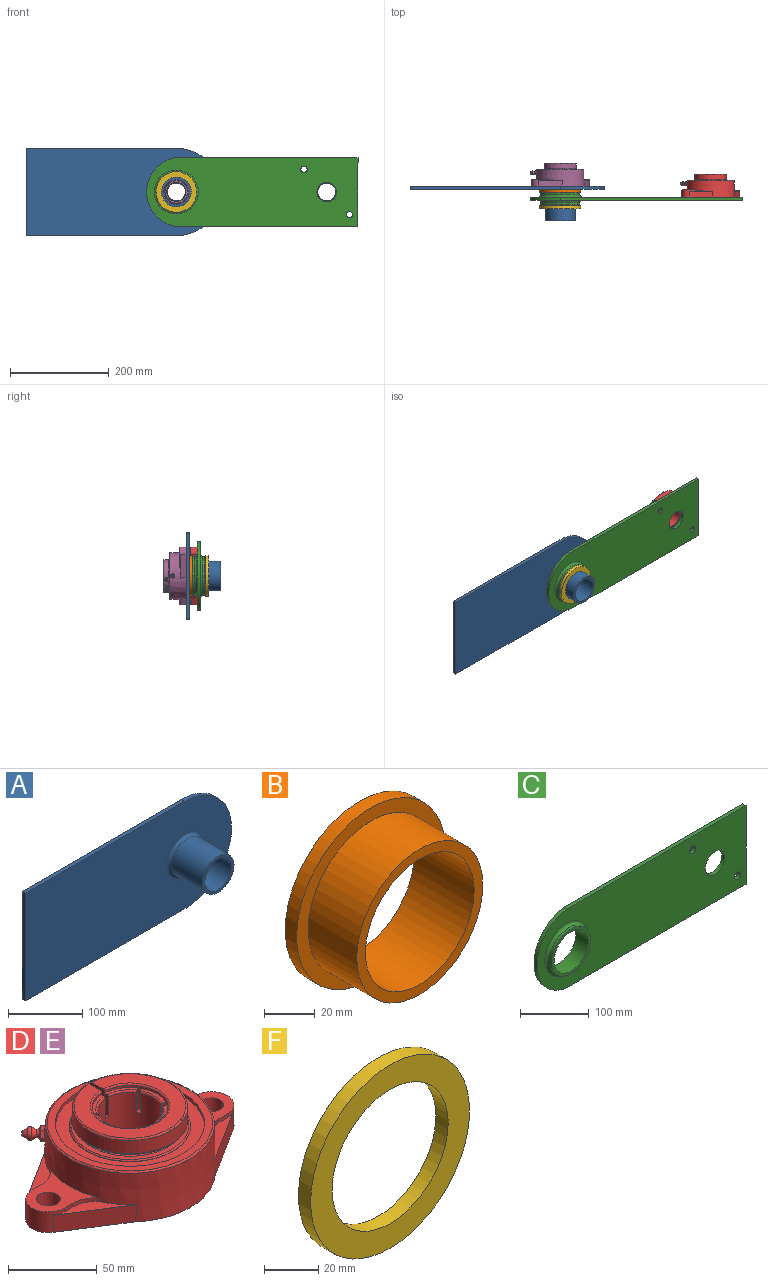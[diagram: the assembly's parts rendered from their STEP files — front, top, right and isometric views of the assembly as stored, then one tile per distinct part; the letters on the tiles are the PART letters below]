
ASSEMBLY  parts=6 mates=12
PART A: 10 faces, bbox 393.7x69.9x177.8 mm
  f0: plane 304.8x6.35mm, normal (0,0,-1), area 1935.5mm2, adj f1,f3,f4,f5
  f1: cylinder r=88.9mm len=177.8mm, axis (0,1,0), area 1773.5mm2, adj f0,f2,f4,f5
  f2: plane 304.8x6.35mm, normal (0,0,1), area 1935.5mm2, adj f1,f3,f4,f5
  f3: plane 177.8x6.35mm, normal (-1,0,0), area 1129mm2, adj f0,f2,f4,f5
  f4: plane 393.7x177.8mm, normal (0,-1,0), area 62775.8mm2, adj f0,f1,f2,f3,f9
  f5: plane 393.7x177.8mm, normal (0,1,0), area 64580.9mm2, adj f0,f1,f2,f3,f6
  f6: cylinder r=25.4mm len=69.85mm, axis (0,1,0), area 11147.6mm2, adj f5,f8
  f7: cylinder r=30.16mm len=60.33mm, axis (0,1,0), area 11131.7mm2, adj f8,f9
  f8: plane 60.33x60.33mm, normal (0,-1,0), area 831.3mm2, adj f6,f7
  f9: torus R=34.92mm, axis (0,-1,0), area 1499.1mm2, adj f4,f7
PART B: 6 faces, bbox 82.6x33.3x82.6 mm
  f0: cylinder r=30.16mm len=60.33mm, axis (0,1,0), area 6318mm2, adj f2,f3
  f1: cylinder r=34.92mm len=69.85mm, axis (0,1,0), area 5922.1mm2, adj f2,f5
  f2: plane 69.85x69.85mm, normal (0,-1,0), area 973.8mm2, adj f0,f1
  f3: plane 82.55x82.55mm, normal (0,1,0), area 2494mm2, adj f0,f4
  f4: cylinder r=41.27mm len=82.55mm, axis (0,1,0), area 1646.8mm2, adj f3,f5
  f5: plane 82.55x82.55mm, normal (0,-1,0), area 1520.1mm2, adj f1,f4
PART C: 16 faces, bbox 428.6x25.4x139.7 mm
  f0: plane 139.7x6.35mm, normal (1,0,0), area 887.1mm2, adj f1,f4,f5,f6
  f1: plane 368.3x6.35mm, normal (0,0,1), area 2338.7mm2, adj f0,f2,f5,f6
  f2: cylinder r=70.6mm len=139.7mm, axis (0,1,0), area 1277.5mm2, adj f1,f4,f5,f6
  f3: cylinder r=19.84mm len=39.69mm, axis (0,1,0), area 791.7mm2, adj f5,f6
  f4: plane 368.3x6.35mm, normal (0,0,-1), area 2338.7mm2, adj f0,f2,f5,f6
  f5: plane 428.63x139.7mm, normal (0,-1,0), area 50137.8mm2, adj f0,f1,f2,f3,f4,f13,f14,f15
  f6: plane 428.63x139.7mm, normal (0,1,0), area 50137.8mm2, adj f0,f1,f2,f3,f4,f12,f14,f15
  f7: cylinder r=39.69mm len=79.38mm, axis (0,1,0), area 1187.6mm2, adj f11,f12
  f8: cylinder r=34.92mm len=69.85mm, axis (0,1,0), area 5573.8mm2, adj f10,f11
  f9: cylinder r=39.69mm len=79.38mm, axis (0,1,0), area 1187.6mm2, adj f10,f13
  f10: plane 79.38x79.38mm, normal (0,-1,0), area 1116.3mm2, adj f8,f9
  f11: plane 79.38x79.38mm, normal (0,1,0), area 1116.3mm2, adj f7,f8
  f12: torus R=44.45mm, axis (0,-1,0), area 1946.8mm2, adj f6,f7
  f13: torus R=44.45mm, axis (0,-1,0), area 1946.8mm2, adj f5,f9
  f14: cylinder r=6.35mm len=12.7mm, axis (0,1,0), area 253.4mm2, adj f5,f6
  f15: cylinder r=6.35mm len=12.7mm, axis (0,1,0), area 253.4mm2, adj f5,f6
PART D: 121 faces, bbox 155.7x103.3x63.6 mm
  f0: plane 2.54x1.8mm, normal (-0.71,0.71,0), area 5.1mm2, adj f1
  f1: torus R=1.27mm, axis (-0.71,0.71,0), area 6.6mm2, adj f0,f2
  f2: cone r=3.57mm half-angle=30deg, axis (0.71,-0.71,0), area 59.1mm2, adj f1,f3
  f3: torus R=1.78mm, axis (-0.71,0.71,0), area 42.7mm2, adj f2,f4
  f4: cone r=2.49mm half-angle=20deg, axis (-0.71,0.71,0), area 70.1mm2, adj f3,f5
  f5: torus R=3.68mm, axis (-0.71,0.71,0), area 42.8mm2, adj f4,f10
  f6: cone r=4.59mm half-angle=60deg, axis (0.71,-0.71,0), area 0.8mm2, adj f10,f13,f15
  f7: cone r=4.59mm half-angle=60deg, axis (0.71,-0.71,0), area 0.8mm2, adj f10,f15,f17
  f8: cone r=4.59mm half-angle=60deg, axis (0.71,-0.71,0), area 0.8mm2, adj f10,f17,f19
  f9: cone r=4.59mm half-angle=60deg, axis (0.71,-0.71,0), area 0.8mm2, adj f10,f19,f21
  f10: plane 7.94x5.75mm, normal (-0.71,0.71,0), area 8.6mm2, adj f5,f6,f7,f8,f9,f11,f12,f13
  f11: cone r=4.59mm half-angle=60deg, axis (0.71,-0.71,0), area 0.8mm2, adj f10,f13,f23
  f12: cone r=4.59mm half-angle=60deg, axis (0.71,-0.71,0), area 0.8mm2, adj f10,f21,f23
  f13: plane 4.11x3.14mm, normal (-0.61,-0.61,-0.5), area 10.9mm2, adj f6,f10,f11,f14,f15,f23,f24,f25
  f14: cone r=4.06mm half-angle=60deg, axis (-0.71,0.71,0), area 0.8mm2, adj f13,f15,f25
  f15: plane 4.11x3.14mm, normal (-0.61,-0.61,0.5), area 10.9mm2, adj f6,f7,f10,f13,f14,f16,f17,f25
  f16: cone r=4.06mm half-angle=60deg, axis (-0.71,0.71,0), area 0.8mm2, adj f15,f17,f25
  f17: plane 4.76x4.76mm, normal (0,0,1), area 10.9mm2, adj f7,f8,f10,f15,f16,f18,f19,f25
  f18: cone r=4.06mm half-angle=60deg, axis (-0.71,0.71,0), area 0.8mm2, adj f17,f19,f25
  f19: plane 4.11x3.14mm, normal (0.61,0.61,0.5), area 10.9mm2, adj f8,f9,f10,f17,f18,f20,f21,f25
  f20: cone r=4.06mm half-angle=60deg, axis (-0.71,0.71,0), area 0.8mm2, adj f19,f21,f25
  f21: plane 4.11x3.14mm, normal (0.61,0.61,-0.5), area 10.9mm2, adj f9,f10,f12,f19,f20,f22,f23,f25
  f22: cone r=4.06mm half-angle=60deg, axis (-0.71,0.71,0), area 0.8mm2, adj f21,f23,f25
  f23: plane 4.76x4.76mm, normal (0,0,-1), area 10.9mm2, adj f10,f11,f12,f13,f21,f22,f24,f25
  f24: cone r=4.06mm half-angle=60deg, axis (-0.71,0.71,0), area 0.8mm2, adj f13,f23,f25
  f25: plane 7.94x5.75mm, normal (0.71,-0.71,0), area 19.5mm2, adj f13,f14,f15,f16,f17,f18,f19,f20
  f26: plane 93.25x93.25mm, normal (0,0,1), area 1269.9mm2, adj f33,f43
  f27: plane 6.8x2.54mm, normal (0,-1,0), area 17.3mm2, adj f31,f32,f42,f45
  f28: plane 6.8x2.54mm, normal (0,1,0), area 17.3mm2, adj f29,f30,f42,f45
  f29: plane 41.19x26.19mm, normal (0,0,1), area 209.4mm2, adj f28,f30,f44,f45,f47
  f30: cylinder r=18.48mm len=14.65mm, axis (0,0,1), area 42.7mm2, adj f28,f29,f42,f47
  f31: cylinder r=18.48mm len=14.65mm, axis (0,0,1), area 42.7mm2, adj f27,f32,f42,f47
  f32: plane 41.19x26.19mm, normal (0,0,1), area 209.4mm2, adj f27,f31,f45,f46,f47
  f33: torus R=46.63mm, axis (0,0,-1), area 468.7mm2, adj f26,f47
  f34: cylinder r=18.48mm len=14.65mm, axis (0,0,1), area 42.7mm2, adj f38,f39,f41,f47
  f35: cylinder r=18.48mm len=14.65mm, axis (0,0,1), area 42.7mm2, adj f37,f40,f41,f47
  f36: cylinder r=3.17mm len=6.35mm, axis (-0.71,0.71,0), area 8.5mm2, adj f25,f47
  f37: plane 6.8x2.54mm, normal (0,1,0), area 17.3mm2, adj f35,f40,f41,f49
  f38: plane 6.8x2.54mm, normal (0,-1,0), area 17.3mm2, adj f34,f39,f41,f49
  f39: plane 41.19x26.19mm, normal (0,0,1), area 209.4mm2, adj f34,f38,f47,f48,f49
  f40: plane 41.19x26.19mm, normal (0,0,1), area 209.4mm2, adj f35,f37,f47,f49,f50
  f41: plane 39.82x34.14mm, normal (0,0,1), area 602.9mm2, adj f34,f35,f37,f38,f47,f49,f51
  f42: plane 39.82x34.14mm, normal (0,0,1), area 602.9mm2, adj f27,f28,f30,f31,f45,f47,f52
  f43: cylinder r=42.07mm len=84.14mm, axis (0,0,-1), area 638.3mm2, adj f26,f53
  f44: plane 41.19x26.19mm, normal (0.54,0.84,0), area 564.6mm2, adj f29,f45,f47,f54
  f45: cylinder r=12.7mm len=25.4mm, axis (0,0,1), area 401mm2, adj f27,f28,f29,f32,f42,f44,f46,f54
  f46: plane 41.19x26.19mm, normal (0.54,-0.84,0), area 564.6mm2, adj f32,f45,f47,f54
  f47: cone r=47.64mm half-angle=1deg, axis (0,0,-1), area 7792.6mm2, adj f29,f30,f31,f32,f33,f34,f35,f36
  f48: plane 41.19x26.19mm, normal (-0.54,-0.84,0), area 564.6mm2, adj f39,f47,f49,f54
  f49: cylinder r=12.7mm len=25.4mm, axis (0,0,1), area 401mm2, adj f37,f38,f39,f40,f41,f48,f50,f54
  f50: plane 41.19x26.19mm, normal (-0.54,0.84,0), area 564.6mm2, adj f40,f47,f49,f54
  f51: cylinder r=6.75mm len=14.29mm, axis (0,0,1), area 605.7mm2, adj f41,f54
  f52: cylinder r=6.75mm len=14.29mm, axis (0,0,1), area 605.7mm2, adj f42,f54
  f53: plane 84.14x84.14mm, normal (0,0,1), area 1874.2mm2, adj f43,f56
  f54: plane 155.58x96.44mm, normal (0,0,-1), area 3750.6mm2, adj f44,f45,f46,f47,f48,f49,f50,f51
  f55: plane 6.35x6.35mm, normal (1,0,0), area 31.7mm2, adj f58
  f56: sphere r=36mm, area 28.8mm2, adj f53,f59
  f57: torus R=32.48mm, axis (0,0,-1), area 3286.8mm2, adj f54,f60
  f58: cone r=3.17mm half-angle=60deg, axis (-1,0,0), area 20.6mm2, adj f55,f62
  f59: torus R=33.25mm, axis (0,0,1), area 270.7mm2, adj f56,f63
  f60: torus R=33.25mm, axis (0,0,1), area 270.7mm2, adj f57,f64
  f61: plane 3.86x3.86mm, normal (-1,0,0), area 11.7mm2, adj f65
  f62: cylinder r=3.97mm len=7.94mm, axis (-1,0,0), area 108.9mm2, adj f58,f66
  f63: plane 66.49x66.49mm, normal (0,0,1), area 621.5mm2, adj f59,f67
  f64: plane 66.49x66.49mm, normal (0,0,-1), area 621.5mm2, adj f60,f68
  f65: cone r=2.41mm half-angle=45deg, axis (1,0,0), area 9.3mm2, adj f61,f69
  f66: plane 9.53x9.53mm, normal (1,0,0), area 21.8mm2, adj f62,f70
  f67: cone r=30.12mm half-angle=86deg, axis (0,0,-1), area 1101.5mm2, adj f63,f72
  f68: cone r=23.61mm half-angle=86deg, axis (0,0,1), area 1101.5mm2, adj f64,f73
  f69: cylinder r=2.41mm len=7.59mm, axis (1,0,0), area 61.5mm2, adj f65,f74
  f70: cylinder r=4.76mm len=18.95mm, axis (1,0,0), area 362.1mm2, adj f66,f74,f77,f78,f79
  f71: plane 5.08x5.08mm, normal (-1,0,0), area 2mm2, adj f75,f81
  f72: cylinder r=23.61mm len=47.23mm, axis (0,0,1), area 285.8mm2, adj f67,f76,f82
  f73: cylinder r=23.61mm len=47.23mm, axis (0,0,1), area 841.7mm2, adj f68,f83
  f74: cylinder r=32.54mm len=65.09mm, axis (0,0,1), area 1585.8mm2, adj f69,f70,f77,f79,f86
  f75: cylinder r=2.41mm len=5.91mm, axis (-1,0,0), area 89.6mm2, adj f71,f86
  f76: plane 63.08x63.04mm, normal (0,0,-1), area 1353.5mm2, adj f72,f77,f86,f88
  f77: torus R=31.53mm, axis (0,0,1), area 318.6mm2, adj f70,f74,f76,f78,f86,f88
  f78: cylinder r=32.54mm len=14.76mm, axis (0,0,1), area 82.6mm2, adj f70,f77,f79,f88
  f79: torus R=31.53mm, axis (0,0,1), area 318.4mm2, adj f70,f74,f78,f80,f86,f88
  f80: plane 63.08x63.04mm, normal (0,0,1), area 1520.3mm2, adj f79,f86,f87,f88
  f81: cylinder r=2.54mm len=5.08mm, axis (1,0,0), area 59.7mm2, adj f71,f88
  f82: plane 2.21x2.17mm, normal (0,0,1), area 4.7mm2, adj f72,f86,f88,f104
  f83: torus R=22.6mm, axis (0,0,1), area 233.1mm2, adj f73,f92
  f84: plane 16.61x10.67mm, normal (0,0,1), area 40.5mm2, adj f98,f99,f100,f104
  f85: plane 16.61x10.67mm, normal (0,0,1), area 40.5mm2, adj f94,f95,f96,f104
  f86: plane 11.14x11.13mm, normal (1,0,0), area 104.6mm2, adj f74,f75,f76,f77,f79,f80,f82,f87
  f87: torus R=22.45mm, axis (0,0,1), area 215.2mm2, adj f80,f86,f88,f104
  f88: plane 11.14x11.13mm, normal (-1,0,0), area 102.7mm2, adj f76,f77,f78,f79,f80,f81,f82,f87
  f89: plane 16.61x10.67mm, normal (0,0,1), area 40.5mm2, adj f104,f107,f108,f109
  f90: plane 16.61x10.67mm, normal (0,0,1), area 40.5mm2, adj f104,f111,f112,f113
  f91: plane 19.18x4.14mm, normal (0,0,1), area 40.5mm2, adj f102,f104,f115,f116
  f92: plane 45.2x45.2mm, normal (0,0,-1), area 437.4mm2, adj f83,f117
  f93: plane 4.03x3.8mm, normal (0,0,1), area 8.1mm2, adj f94,f102,f104,f120
  f94: plane 14.63x2.78mm, normal (-0.5,0.87,0), area 46.2mm2, adj f85,f93,f95,f104,f120
  f95: torus R=19.27mm, axis (0,0,1), area 27.1mm2, adj f85,f94,f96,f120
  f96: plane 14.63x3.21mm, normal (1,0,0), area 46.2mm2, adj f85,f95,f97,f104,f120
  f97: plane 3.22x2.56mm, normal (0,0,1), area 8.1mm2, adj f96,f98,f104,f120
  f98: plane 14.63x3.21mm, normal (-1,0,0), area 46.2mm2, adj f84,f97,f99,f104,f120
  f99: torus R=19.27mm, axis (0,0,1), area 27.1mm2, adj f84,f98,f100,f120
  f100: plane 14.63x2.78mm, normal (0.5,0.87,0), area 46.2mm2, adj f84,f99,f101,f104,f120
  f101: plane 4.03x3.8mm, normal (0,0,1), area 8.1mm2, adj f100,f103,f104,f120
  f102: plane 14.63x2.78mm, normal (0.5,-0.87,0), area 46.2mm2, adj f91,f93,f104,f116,f120
  f103: plane 14.63x2.78mm, normal (-0.5,-0.87,0), area 46.2mm2, adj f101,f104,f105,f118,f120
  f104: cylinder r=21.43mm len=42.86mm, axis (0,0,1), area 393.1mm2, adj f82,f84,f85,f86,f87,f88,f89,f90
  f105: plane 19.18x4.14mm, normal (0,0,1), area 40.5mm2, adj f103,f104,f118,f119
  f106: plane 4.03x3.8mm, normal (0,0,1), area 8.1mm2, adj f104,f107,f119,f120
  f107: plane 14.63x2.78mm, normal (0.5,-0.87,0), area 46.2mm2, adj f89,f104,f106,f108,f120
  f108: torus R=19.27mm, axis (0,0,1), area 27.1mm2, adj f89,f107,f109,f120
  f109: plane 14.63x3.21mm, normal (-1,0,0), area 46.2mm2, adj f89,f104,f108,f110,f120
  f110: plane 3.22x2.56mm, normal (0,0,1), area 8.1mm2, adj f104,f109,f111,f120
  f111: plane 14.63x3.21mm, normal (1,0,0), area 46.2mm2, adj f90,f104,f110,f112,f120
  f112: torus R=19.27mm, axis (0,0,1), area 27.1mm2, adj f90,f111,f113,f120
  f113: plane 14.63x2.78mm, normal (-0.5,-0.87,0), area 46.2mm2, adj f90,f104,f112,f114,f120
  f114: plane 4.03x3.8mm, normal (0,0,1), area 8.1mm2, adj f104,f113,f115,f120
  f115: plane 14.63x2.78mm, normal (0.5,0.87,0), area 46.2mm2, adj f91,f104,f114,f116,f120
  f116: torus R=19.27mm, axis (0,0,1), area 27.1mm2, adj f91,f102,f115,f120
  f117: torus R=19.27mm, axis (0,0,1), area 186.8mm2, adj f92,f120
  f118: torus R=19.27mm, axis (0,0,1), area 27.1mm2, adj f103,f105,f119,f120
  f119: plane 14.63x2.78mm, normal (-0.5,0.87,0), area 46.2mm2, adj f104,f105,f106,f118,f120
  f120: cylinder r=18.26mm len=39.98mm, axis (0,0,1), area 4377.9mm2, adj f93,f94,f95,f96,f97,f98,f99,f100
PART E: same geometry as D
PART F: 4 faces, bbox 82.6x6.4x82.6 mm
  f0: cylinder r=30.16mm len=60.33mm, axis (0,1,0), area 1203.4mm2, adj f2,f3
  f1: cylinder r=41.27mm len=82.55mm, axis (0,1,0), area 1646.8mm2, adj f2,f3
  f2: plane 82.55x82.55mm, normal (0,-1,0), area 2494mm2, adj f0,f1
  f3: plane 82.55x82.55mm, normal (0,1,0), area 2494mm2, adj f0,f1
PLACE A rot(axis=(0,1,0),0deg) t=(112.92,44.48,34.12)mm
PLACE B t=(112.92,38.13,34.12)mm
PLACE C rot(axis=(0,1,0),0deg) t=(265.32,19.08,34.12)mm
PLACE D rot(axis=(-0.86,0.36,0.36),98.4deg) t=(417.72,42.89,34.12)mm
PLACE E rot(axis=(-0.86,0.36,0.36),98.4deg) t=(112.92,65.12,34.12)mm
PLACE F t=(112.92,4.79,34.12)mm
MATE planar E.f54 <-> A.f5  axis (0,-1,0) through (59.64,44.48,54.27)mm
MATE cylindrical D.f33 <-> C.f3  axis (0,1,0) through (417.72,64.84,34.12)mm
MATE planar D.f49 <-> C.f6  axis (0,-1,0) through (371.7,22.26,80.14)mm
MATE cylindrical C.f15 <-> D.f45  axis (0,1,0) through (463.74,19.08,-11.9)mm
MATE cylindrical A.f7 <-> B.f1  axis (0,1,0) through (112.92,4,34.12)mm
MATE cylindrical C.f8 <-> B.f1  axis (0,1,0) through (112.92,6.38,34.12)mm
MATE cylindrical E.f33 <-> A.f6  axis (0,1,0) through (112.92,87.07,34.12)mm
MATE planar F.f1 <-> B.f4  axis (0,1,0) through (112.92,4.79,34.12)mm
MATE planar B.f4 <-> A.f4  axis (0,1,0) through (112.92,38.13,34.12)mm
MATE cylindrical C.f14 <-> D.f49  axis (0,1,0) through (371.7,19.08,80.14)mm
MATE cylindrical F.f0 <-> A.f7  axis (0,1,0) through (112.92,1.62,34.12)mm
MATE planar C.f7 <-> B.f4  axis (0,1,0) through (112.92,31.78,34.12)mm
